# Revit family: 306_5ce6cf51bd6b4c28849451227ff038
name_source: partatom
category: Pipe Accessories
units: mm (PartAtom-declared; Revit-internal decimal feet)

## family parameters
Always vertical = Yes
Cut with Voids When Loaded = No
Part Type = Valve - Breaks Into
Round Connector Dimension = Use Diameter
Shared = No
Work Plane-Based = No

## types (17) — shared parameters
CAT0 = Yes
D10 = 15 mm  [stored 0.0492126 ft]
Description = 2-way Control valve VLE325, PN16 flange
H3 = 36 mm  [stored 0.11811 ft]
H4 = 24 mm  [stored 0.0787402 ft]
L2D_Min = 3048 mm
Manufacturer = ESBE
QmdConnectorList = 301;D;302;D
URL = http://www.esbe.eu
XN1 = 3 mm  [stored 0.00984252 ft]
Z1 = 14 mm  [stored 0.0459318 ft]
Z11 = 6 mm  [stored 0.019685 ft]
Z2 = 36 mm  [stored 0.11811 ft]
Z4 = 13 mm
Z5 = 4 mm  [stored 0.0131234 ft]
Z6 = 2 mm  [stored 0.00656168 ft]
Z7 = 15 mm  [stored 0.0492126 ft]
magiPartTypeId = 306
magiProductFamilyId = 5ce6cf51bd6b4c28849451227ff038

## per-type parameters (varying)
| type | CenSd_D6_6 | D | D1 | D13 | D2 | D3 | D4 | D5 | D6 | D7 | D8 | D9 | DN3 | DN4 | FDT2 | L2 | L2D | LT2 | W2D | X1 | XN | XN2 | XN2__ve | magiProductId |
| VLE325 PN16 FLANGE DN20-0,63 | 18 mm  [stored 0.0590551 ft] | 20 mm | 40 mm | 17 mm | 32 mm | 29 mm | 26 mm | 27 mm | 21 mm  [stored 0.0688976 ft] | 14 mm  [stored 0.0459318 ft] | 4 mm  [stored 0.0131234 ft] | 4 mm  [stored 0.0131234 ft] | 12 mm  [stored 0.0393701 ft] | 25 mm  [stored 0.082021 ft] | 53 mm | 106 mm | 143 mm | 72 mm | 20 mm  [stored 0.0656168 ft] | 4 mm  [stored 0.0131234 ft] | 14 mm  [stored 0.0459318 ft] | 11 mm | -11 mm | 0d4d856bd4cc4f299a1e5c0824862b |
| VLE325 PN16 FLANGE DN40-6,3 | 21 mm  [stored 0.0688976 ft] | 40 mm | 48 mm | 21 mm  [stored 0.0688976 ft] | 38 mm | 34 mm | 31 mm | 33 mm | 24 mm  [stored 0.0787402 ft] | 17 mm | 5 mm  [stored 0.0164042 ft] | 5 mm  [stored 0.0164042 ft] | 24 mm  [stored 0.0787402 ft] | 50 mm | 75 mm | 126 mm | 170 mm | 85 mm | 40 mm | 5 mm  [stored 0.0164042 ft] | 17 mm | 14 mm  [stored 0.0459318 ft] | -14 mm | 8a1363f6b3eb41e6af427485153e16 |
| VLE325 PN16 FLANGE DN40-4,0 | 21 mm  [stored 0.0688976 ft] | 40 mm | 48 mm | 21 mm  [stored 0.0688976 ft] | 38 mm | 34 mm | 31 mm | 33 mm | 24 mm  [stored 0.0787402 ft] | 17 mm | 5 mm  [stored 0.0164042 ft] | 5 mm  [stored 0.0164042 ft] | 24 mm  [stored 0.0787402 ft] | 50 mm | 75 mm | 126 mm | 170 mm | 85 mm | 40 mm | 5 mm  [stored 0.0164042 ft] | 17 mm | 14 mm  [stored 0.0459318 ft] | -14 mm | b0ca9b41e0574d47996ce06f7c2c74 |
| VLE325 PN16 FLANGE DN40-2,5 | 21 mm  [stored 0.0688976 ft] | 40 mm | 48 mm | 21 mm  [stored 0.0688976 ft] | 38 mm | 34 mm | 31 mm | 33 mm | 24 mm  [stored 0.0787402 ft] | 17 mm | 5 mm  [stored 0.0164042 ft] | 5 mm  [stored 0.0164042 ft] | 24 mm  [stored 0.0787402 ft] | 50 mm | 75 mm | 126 mm | 170 mm | 85 mm | 40 mm | 5 mm  [stored 0.0164042 ft] | 17 mm | 14 mm  [stored 0.0459318 ft] | -14 mm | e2f95fdb151f41429c950451fa5c38 |
| VLE325 PN16 FLANGE DN40-1,6 | 21 mm  [stored 0.0688976 ft] | 40 mm | 48 mm | 21 mm  [stored 0.0688976 ft] | 38 mm | 34 mm | 31 mm | 33 mm | 24 mm  [stored 0.0787402 ft] | 17 mm | 5 mm  [stored 0.0164042 ft] | 5 mm  [stored 0.0164042 ft] | 24 mm  [stored 0.0787402 ft] | 50 mm | 75 mm | 126 mm | 170 mm | 85 mm | 40 mm | 5 mm  [stored 0.0164042 ft] | 17 mm | 14 mm  [stored 0.0459318 ft] | -14 mm | 13f7c92af02e4436b4306359cc30ec |
| VLE325 PN16 FLANGE DN32-6,3 | 21 mm  [stored 0.0688976 ft] | 32 mm | 46 mm | 20 mm  [stored 0.0656168 ft] | 37 mm | 33 mm | 30 mm  [stored 0.0984252 ft] | 32 mm | 24 mm  [stored 0.0787402 ft] | 17 mm | 5 mm  [stored 0.0164042 ft] | 4 mm  [stored 0.0131234 ft] | 19 mm | 40 mm | 70 mm | 122 mm | 165 mm | 83 mm | 32 mm | 5 mm  [stored 0.0164042 ft] | 17 mm | 13 mm | -13 mm | cd14db5401b24f5ba897f74a19ffdc |
| VLE325 PN16 FLANGE DN32-4,0 | 21 mm  [stored 0.0688976 ft] | 32 mm | 46 mm | 20 mm  [stored 0.0656168 ft] | 37 mm | 33 mm | 30 mm  [stored 0.0984252 ft] | 32 mm | 24 mm  [stored 0.0787402 ft] | 17 mm | 5 mm  [stored 0.0164042 ft] | 4 mm  [stored 0.0131234 ft] | 19 mm | 40 mm | 70 mm | 122 mm | 165 mm | 83 mm | 32 mm | 5 mm  [stored 0.0164042 ft] | 17 mm | 13 mm | -13 mm | 8faf9efcf36d4769949d12b2a5505d |
| VLE325 PN16 FLANGE DN32-2,5 | 21 mm  [stored 0.0688976 ft] | 32 mm | 46 mm | 20 mm  [stored 0.0656168 ft] | 37 mm | 33 mm | 30 mm  [stored 0.0984252 ft] | 32 mm | 24 mm  [stored 0.0787402 ft] | 17 mm | 5 mm  [stored 0.0164042 ft] | 4 mm  [stored 0.0131234 ft] | 19 mm | 40 mm | 70 mm | 122 mm | 165 mm | 83 mm | 32 mm | 5 mm  [stored 0.0164042 ft] | 17 mm | 13 mm | -13 mm | d860500f427441aa9e8accff3da6b3 |
| VLE325 PN16 FLANGE DN32-1,6 | 21 mm  [stored 0.0688976 ft] | 32 mm | 46 mm | 20 mm  [stored 0.0656168 ft] | 37 mm | 33 mm | 30 mm  [stored 0.0984252 ft] | 32 mm | 24 mm  [stored 0.0787402 ft] | 17 mm | 5 mm  [stored 0.0164042 ft] | 4 mm  [stored 0.0131234 ft] | 19 mm | 40 mm | 70 mm | 122 mm | 165 mm | 83 mm | 32 mm | 5 mm  [stored 0.0164042 ft] | 17 mm | 13 mm | -13 mm | 1936fd0d8a6a4c1e99975aa556934e |
| VLE325 PN16 FLANGE DN25-4,0 | 19 mm | 25 mm | 44 mm | 19 mm | 35 mm | 31 mm | 28 mm | 30 mm  [stored 0.0984252 ft] | 22 mm | 16 mm | 5 mm  [stored 0.0164042 ft] | 4 mm  [stored 0.0131234 ft] | 15 mm  [stored 0.0492126 ft] | 31 mm | 58 mm | 115 mm | 156 mm | 78 mm | 25 mm  [stored 0.082021 ft] | 5 mm  [stored 0.0164042 ft] | 16 mm | 12 mm  [stored 0.0393701 ft] | -12 mm  [stored -0.0393701 ft] | c10b917bb7fc4927afe46a5847e23d |
| VLE325 PN16 FLANGE DN25-2,5 | 19 mm | 25 mm | 44 mm | 19 mm | 35 mm | 31 mm | 28 mm | 30 mm  [stored 0.0984252 ft] | 22 mm | 16 mm | 5 mm  [stored 0.0164042 ft] | 4 mm  [stored 0.0131234 ft] | 15 mm  [stored 0.0492126 ft] | 31 mm | 58 mm | 115 mm | 156 mm | 78 mm | 25 mm  [stored 0.082021 ft] | 5 mm  [stored 0.0164042 ft] | 16 mm | 12 mm  [stored 0.0393701 ft] | -12 mm  [stored -0.0393701 ft] | 9786f725c7164e2c9469f5162f1832 |
| VLE325 PN16 FLANGE DN25-1,6 | 19 mm | 25 mm | 44 mm | 19 mm | 35 mm | 31 mm | 28 mm | 30 mm  [stored 0.0984252 ft] | 22 mm | 16 mm | 5 mm  [stored 0.0164042 ft] | 4 mm  [stored 0.0131234 ft] | 15 mm  [stored 0.0492126 ft] | 31 mm | 58 mm | 115 mm | 156 mm | 78 mm | 25 mm  [stored 0.082021 ft] | 5 mm  [stored 0.0164042 ft] | 16 mm | 12 mm  [stored 0.0393701 ft] | -12 mm  [stored -0.0393701 ft] | 77caa64f893845cc8a7f98652d0275 |
| VLE325 PN16 FLANGE DN25-1,0 | 19 mm | 25 mm | 44 mm | 19 mm | 35 mm | 31 mm | 28 mm | 30 mm  [stored 0.0984252 ft] | 22 mm | 16 mm | 5 mm  [stored 0.0164042 ft] | 4 mm  [stored 0.0131234 ft] | 15 mm  [stored 0.0492126 ft] | 31 mm | 58 mm | 115 mm | 156 mm | 78 mm | 25 mm  [stored 0.082021 ft] | 5 mm  [stored 0.0164042 ft] | 16 mm | 12 mm  [stored 0.0393701 ft] | -12 mm  [stored -0.0393701 ft] | 688bcb20428a4ec4b5e6b8ff72c9c9 |
| VLE325 PN16 FLANGE DN20-4,0 | 18 mm  [stored 0.0590551 ft] | 20 mm | 40 mm | 17 mm | 32 mm | 29 mm | 26 mm | 27 mm | 21 mm  [stored 0.0688976 ft] | 14 mm  [stored 0.0459318 ft] | 4 mm  [stored 0.0131234 ft] | 4 mm  [stored 0.0131234 ft] | 12 mm  [stored 0.0393701 ft] | 25 mm  [stored 0.082021 ft] | 53 mm | 106 mm | 143 mm | 72 mm | 20 mm  [stored 0.0656168 ft] | 4 mm  [stored 0.0131234 ft] | 14 mm  [stored 0.0459318 ft] | 11 mm | -11 mm | 225cc381e857467c9899bf7d639617 |
| VLE325 PN16 FLANGE DN20-2,5 | 18 mm  [stored 0.0590551 ft] | 20 mm | 40 mm | 17 mm | 32 mm | 29 mm | 26 mm | 27 mm | 21 mm  [stored 0.0688976 ft] | 14 mm  [stored 0.0459318 ft] | 4 mm  [stored 0.0131234 ft] | 4 mm  [stored 0.0131234 ft] | 12 mm  [stored 0.0393701 ft] | 25 mm  [stored 0.082021 ft] | 53 mm | 106 mm | 143 mm | 72 mm | 20 mm  [stored 0.0656168 ft] | 4 mm  [stored 0.0131234 ft] | 14 mm  [stored 0.0459318 ft] | 11 mm | -11 mm | 86601d046cca4a5c84abb12f7d7106 |
| VLE325 PN16 FLANGE DN20-1,6 | 18 mm  [stored 0.0590551 ft] | 20 mm | 40 mm | 17 mm | 32 mm | 29 mm | 26 mm | 27 mm | 21 mm  [stored 0.0688976 ft] | 14 mm  [stored 0.0459318 ft] | 4 mm  [stored 0.0131234 ft] | 4 mm  [stored 0.0131234 ft] | 12 mm  [stored 0.0393701 ft] | 25 mm  [stored 0.082021 ft] | 53 mm | 106 mm | 143 mm | 72 mm | 20 mm  [stored 0.0656168 ft] | 4 mm  [stored 0.0131234 ft] | 14 mm  [stored 0.0459318 ft] | 11 mm | -11 mm | 4a9cea405ae64e9faca6504978c3fc |
| VLE325 PN16 FLANGE DN20-1,0 | 18 mm  [stored 0.0590551 ft] | 20 mm | 40 mm | 17 mm | 32 mm | 29 mm | 26 mm | 27 mm | 21 mm  [stored 0.0688976 ft] | 14 mm  [stored 0.0459318 ft] | 4 mm  [stored 0.0131234 ft] | 4 mm  [stored 0.0131234 ft] | 12 mm  [stored 0.0393701 ft] | 25 mm  [stored 0.082021 ft] | 53 mm | 106 mm | 143 mm | 72 mm | 20 mm  [stored 0.0656168 ft] | 4 mm  [stored 0.0131234 ft] | 14 mm  [stored 0.0459318 ft] | 11 mm | -11 mm | 9a2523db840348429d0c811e7cd2a0 |

note: column(s) folded — value = type name in every type: magiProductCode

note: [stored X ft] marks values corroborated as IEEE doubles in the binary element streams (Revit-internal decimal feet)

## geometry (parser evidence)
native form markers: Sweep x3
no freeform markers — native parametric forms only
